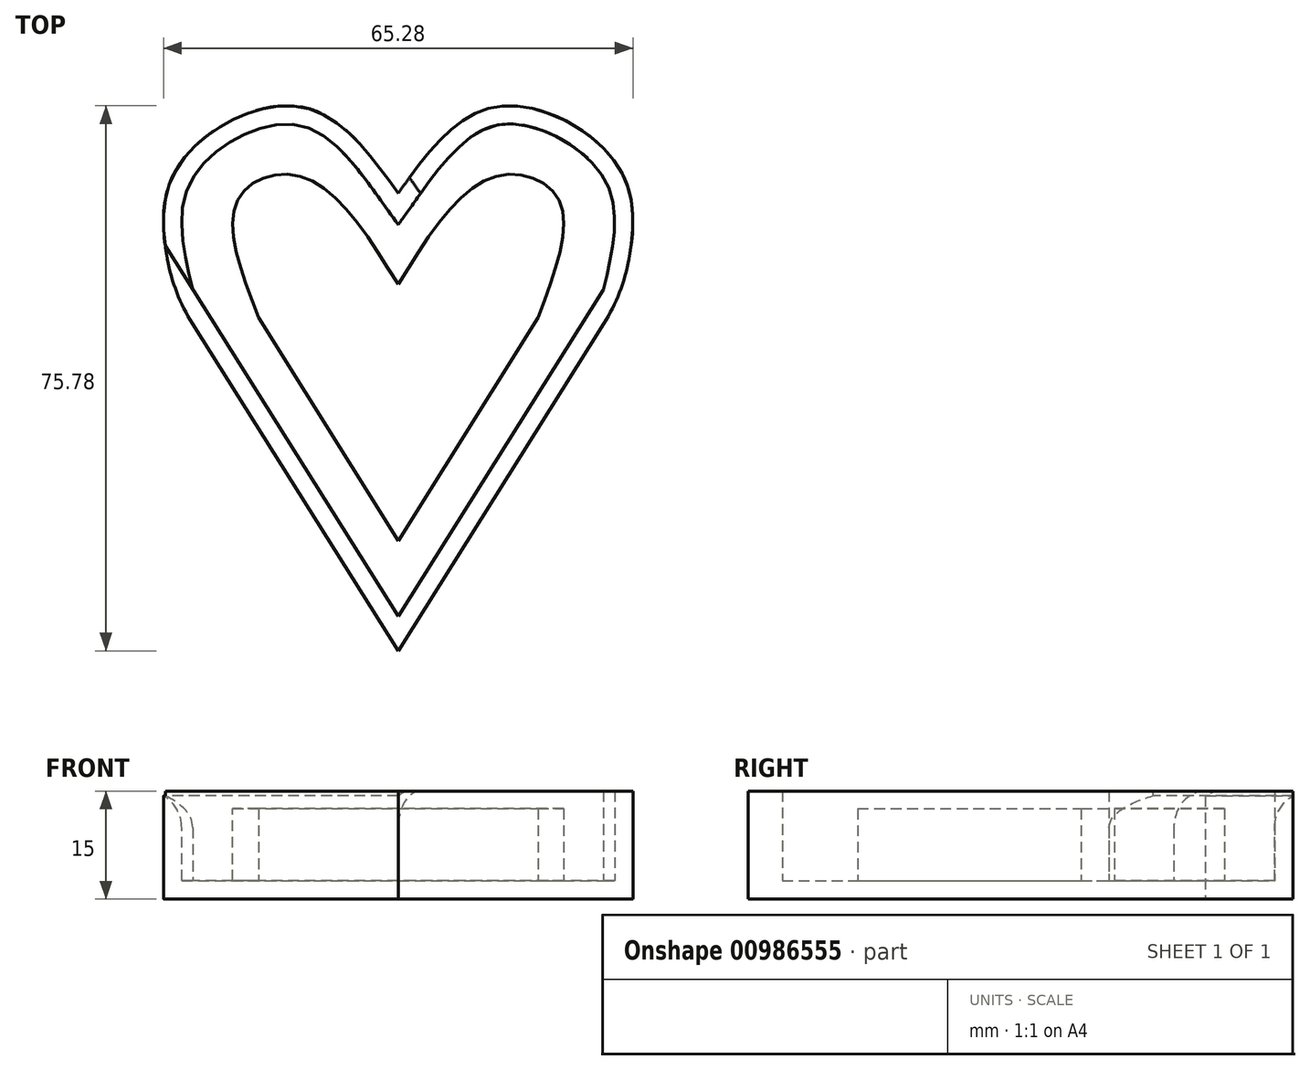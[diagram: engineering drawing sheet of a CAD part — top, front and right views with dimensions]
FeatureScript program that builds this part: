
annotation { "Feature Type Name" : "Feature", "Feature Type Description" : "" }
export const myFeature = defineFeature(function(context is Context, id is Id, definition is map)
    precondition{}
    {
        {
            var Q0;
            Q0=qCreatedBy(makeId("Top.planeOp"),FACE);
            var sketch = newSketch(context, id + "F0", { "sketchPlane" : qUnion([Q0])});
            skLineSegment(sketch, "E0", {"start": v(0, -30.36) * mm, "end": v(-30.94, 18.85) * mm});
            skFitSpline(sketch, "E1", {"points": [v(-30.94, 18.85) * mm, v(-30.94, 36.4) * mm, v(-13.96, 45.33) * mm, v(0, 33.24) * mm], "startDerivative": vector(-13.57, 57.03) * mm, "endDerivative": vector(36.28, -50.84) * mm});
            skFitSpline(sketch, "E2.MirrorCS", {"points": [v(30.94, 18.85) * mm, v(30.94, 36.4) * mm, v(13.96, 45.33) * mm, v(0, 33.24) * mm], "startDerivative": vector(13.57, 57.03) * mm, "endDerivative": vector(-36.28, -50.84) * mm});
            skLineSegment(sketch, "E3.MirrorCS", {"start": v(0, -30.36) * mm, "end": v(30.94, 18.85) * mm});
            skSolve(sketch);
        }
        {
            var Q0;
            Q0=makeQuery(id+"F0.imprint","IMPRINT",FACE,{"disambiguationData":[TD([[makeQuery(id+"F0.imprint","IMPRINT",EDGE,{"derivedFrom":sQuery(id+"F0.wireOp",EDGE,"E0")}),-1.0]])]});
            extrude(context, id + "F1", {"entities" : qUnion([Q0]), "depth" : 15 * mm, "offsetDistance" : 25.4 * mm});
        }
        {
            var Q0;
            Q0=makeQuery(id+"F1.opExtrude","CAP_FACE",FACE,{"disambiguationData":[OSD([sQuery(id+"F0.wireOp",EDGE,"E0"),sQuery(id+"F0.wireOp",EDGE,"E1"),sQuery(id+"F0.wireOp",EDGE,"E2.MirrorCS"),sQuery(id+"F0.wireOp",EDGE,"E3.MirrorCS")])],"isStart":false});
            shell(context, id + "F2", {"entities" : qUnion([Q0]), "thickness" : 2.54 * mm});
        }
        {
            var Q0;
            Q0=makeQuery(id+"F2.opShell","OFFSET_FACE",FACE,{"disambiguationData":[OSD([sQuery(id+"F0.wireOp",EDGE,"E0"),sQuery(id+"F0.wireOp",EDGE,"E1"),sQuery(id+"F0.wireOp",EDGE,"E2.MirrorCS"),sQuery(id+"F0.wireOp",EDGE,"E3.MirrorCS")])]});
            var sketch = newSketch(context, id + "F3", { "sketchPlane" : qUnion([Q0])});
            skLineSegment(sketch, "E4", {"start": v(0, -15.1) * mm, "end": v(-19.43, 15.97) * mm});
            skFitSpline(sketch, "E5", {"points": [v(-19.43, 15.97) * mm, v(-22.3, 32.38) * mm, v(-13.38, 35.54) * mm, v(0, 20.58) * mm], "startDerivative": vector(-20.65, 54.08) * mm, "endDerivative": vector(32.28, -52.32) * mm});
            skFitSpline(sketch, "E6.MirrorCS", {"points": [v(19.43, 15.97) * mm, v(22.3, 32.38) * mm, v(13.38, 35.54) * mm, v(0, 20.58) * mm], "startDerivative": vector(20.65, 54.08) * mm, "endDerivative": vector(-32.28, -52.32) * mm});
            skLineSegment(sketch, "E7.MirrorCS", {"start": v(0, -15.1) * mm, "end": v(19.43, 15.97) * mm});
            skSolve(sketch);
        }
        {
            var Q0;
            Q0=makeQuery(id+"F3.imprint","IMPRINT",FACE,{"disambiguationData":[TD([[makeQuery(id+"F3.imprint","IMPRINT",EDGE,{"derivedFrom":sQuery(id+"F3.wireOp",EDGE,"E4")}),-1.0]])]});
            extrude(context, id + "F4", {"entities" : qUnion([Q0]), "operationType" : NewBodyOperationType.ADD, "depth" : 10 * mm, "offsetDistance" : 25.4 * mm});
        }
        {
            var Q0;
            Q0=makeQuery(id+"F1.opExtrude","SWEPT_EDGE",EDGE,{"disambiguationData":[OSD([sQuery(id+"F0.wireOp",EDGE,"E0"),sQuery(id+"F0.wireOp",EDGE,"E1")])]});
            fillet(context, id + "F5", {"entities" : qUnion([Q0]), "radius" : 25.4 * mm, "tangentPropagation" : true, "allowEdgeOverflow" : false});
        }
        {
            var Q0;
            Q0=makeQuery(id+"F1.opExtrude","SWEPT_EDGE",EDGE,{"disambiguationData":[OSD([sQuery(id+"F0.wireOp",EDGE,"E2.MirrorCS"),sQuery(id+"F0.wireOp",EDGE,"E3.MirrorCS")])]});
            fillet(context, id + "F6", {"entities" : qUnion([Q0]), "radius" : 25.4 * mm, "tangentPropagation" : true, "allowEdgeOverflow" : false});
        }
        {
            var Q0;
            {var subQ0=sQuery(id+"F0.wireOp",EDGE,"E1");Q0=makeQuery(id+"F2.opShell","OFFSET_EDGE",EDGE,{"disambiguationData":[OSD([subQ0]),TDD([makeQuery(id+"F1.opExtrude","CAP_EDGE",EDGE,{"disambiguationData":[OSD([subQ0])],"isStart":false})])]});}
            fillet(context, id + "F7", {"entities" : qUnion([Q0]), "radius" : 5.08 * mm, "tangentPropagation" : true, "allowEdgeOverflow" : false});
        }
    });
